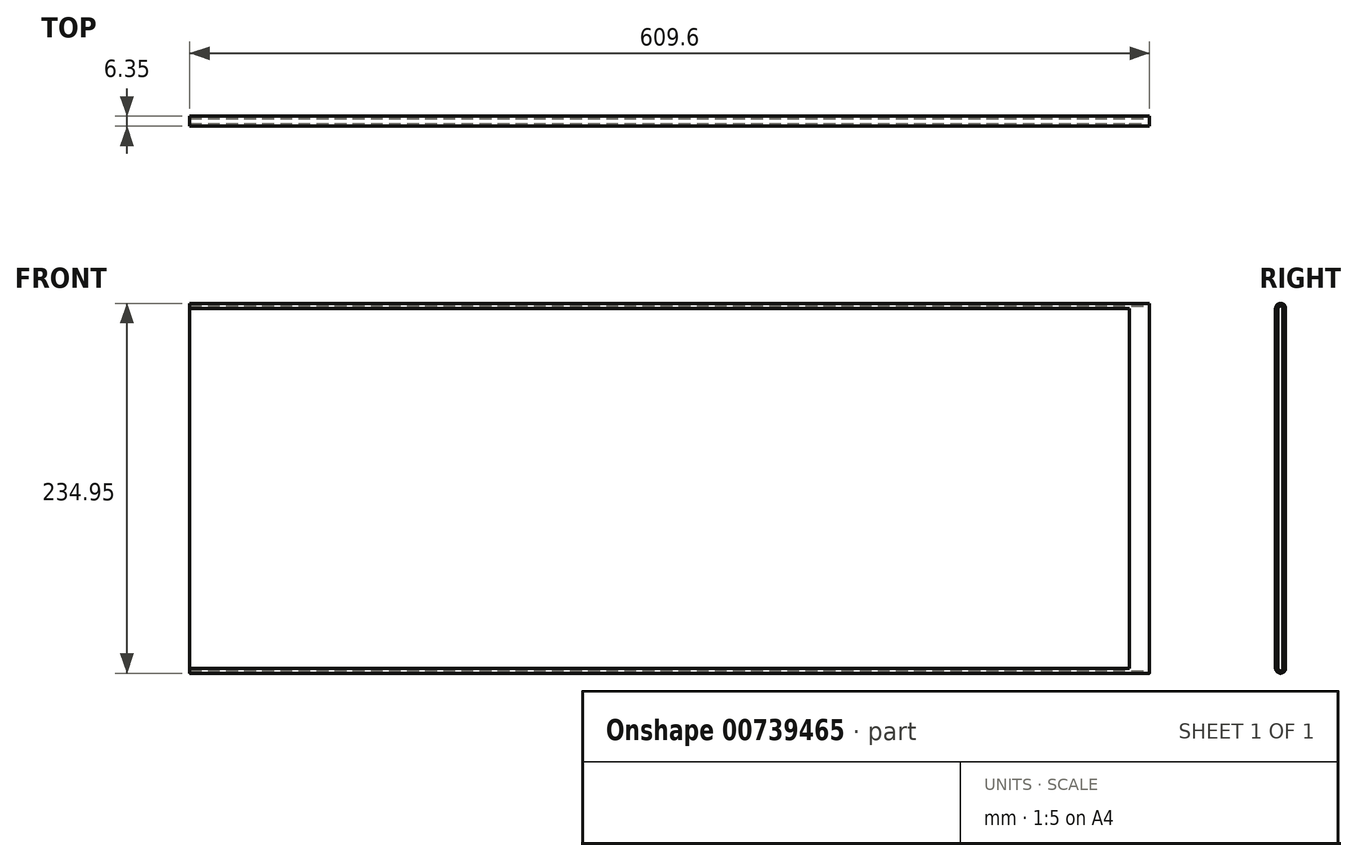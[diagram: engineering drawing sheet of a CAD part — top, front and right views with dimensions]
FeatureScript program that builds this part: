
annotation { "Feature Type Name" : "Feature", "Feature Type Description" : "" }
export const myFeature = defineFeature(function(context is Context, id is Id, definition is map)
    precondition{}
    {
        {
            var Q0;
            Q0=qCreatedBy(makeId("Right.planeOp"),FACE);
            var sketch = newSketch(context, id + "F0", { "sketchPlane" : qUnion([Q0])});
            skLineSegment(sketch, "E0.left", {"start": v(0, -90.43) * mm, "end": v(0, 138.17) * mm});
            skArc(sketch, "E1", {"start": v(-4.76, -90.43) * mm, "mid": v(-3.17, -92.02) * mm, "end": v(-1.59, -90.43) * mm});
            skArc(sketch, "E2", {"start": v(-6.35, -90.43) * mm, "mid": v(-3.17, -93.6) * mm, "end": v(0, -90.43) * mm});
            skLineSegment(sketch, "E3", {"start": v(-1.59, -90.43) * mm, "end": v(-1.59, -90.43) * mm});
            skArc(sketch, "E4", {"start": v(-1.59, 138.17) * mm, "mid": v(-3.18, 139.76) * mm, "end": v(-4.76, 138.17) * mm});
            skArc(sketch, "E5", {"start": v(0, 138.17) * mm, "mid": v(-3.18, 141.35) * mm, "end": v(-6.35, 138.17) * mm});
            skLineSegment(sketch, "E6.right", {"start": v(-1.59, 138.17) * mm, "end": v(-1.59, -90.43) * mm});
            skLineSegment(sketch, "E7", {"start": v(-6.35, 138.17) * mm, "end": v(-4.76, 138.17) * mm});
            skLineSegment(sketch, "E8", {"start": v(-6.35, -90.43) * mm, "end": v(-4.76, -90.43) * mm});
            skLineSegment(sketch, "E9.left", {"start": v(-6.35, 138.17) * mm, "end": v(-6.35, -90.43) * mm});
            skLineSegment(sketch, "E9.right", {"start": v(-4.76, 138.17) * mm, "end": v(-4.76, -90.43) * mm});
            skSolve(sketch);
        }
        {
            var Q0;
            Q0=makeQuery(id+"F0.imprint","IMPRINT",FACE,{"disambiguationData":[TD([[makeQuery(id+"F0.imprint","IMPRINT",EDGE,{"derivedFrom":sQuery(id+"F0.wireOp",EDGE,"E0.left")}),1.0]])]});
            var Q1;
            Q1=makeQuery(id+"F0.imprint","IMPRINT",FACE,{"disambiguationData":[TD([[makeQuery(id+"F0.imprint","IMPRINT",EDGE,{"derivedFrom":sQuery(id+"F0.wireOp",EDGE,"E7")}),-1.0]])]});
            extrude(context, id + "F1", {"entities" : qUnion([Q0, Q1]), "oppositeDirection" : true, "depth" : 609.6 * mm, "offsetDistance" : 25.4 * mm});
        }
        {
            var Q0;
            Q0=makeQuery(id+"F1.opExtrude","SWEPT_FACE",FACE,{"disambiguationData":[OSD([sQuery(id+"F0.wireOp",EDGE,"E9.left")])]});
            var sketch = newSketch(context, id + "F2", { "sketchPlane" : qUnion([Q0])});
            skLineSegment(sketch, "E10.bottom", {"start": v(-609.6, 138.17) * mm, "end": v(-12.7, 138.17) * mm});
            skLineSegment(sketch, "E10.top", {"start": v(-609.6, -90.43) * mm, "end": v(-12.7, -90.43) * mm});
            skLineSegment(sketch, "E10.left", {"start": v(-609.6, 138.17) * mm, "end": v(-609.6, -90.43) * mm});
            skLineSegment(sketch, "E10.right", {"start": v(-12.7, 138.17) * mm, "end": v(-12.7, -90.43) * mm});
            skSolve(sketch);
        }
        {
            var Q0;
            Q0=makeQuery(id+"F2.imprint","IMPRINT",FACE,{"disambiguationData":[TD([[makeQuery(id+"F2.imprint","IMPRINT",EDGE,{"derivedFrom":sQuery(id+"F2.wireOp",EDGE,"E10.bottom")}),-1.0]])]});
            extrude(context, id + "F3", {"entities" : qUnion([Q0]), "operationType" : NewBodyOperationType.REMOVE, "endBound" : BoundingType.UP_TO_NEXT, "oppositeDirection" : true, "depth" : 25.4 * mm, "offsetDistance" : 25.4 * mm});
        }
    });
